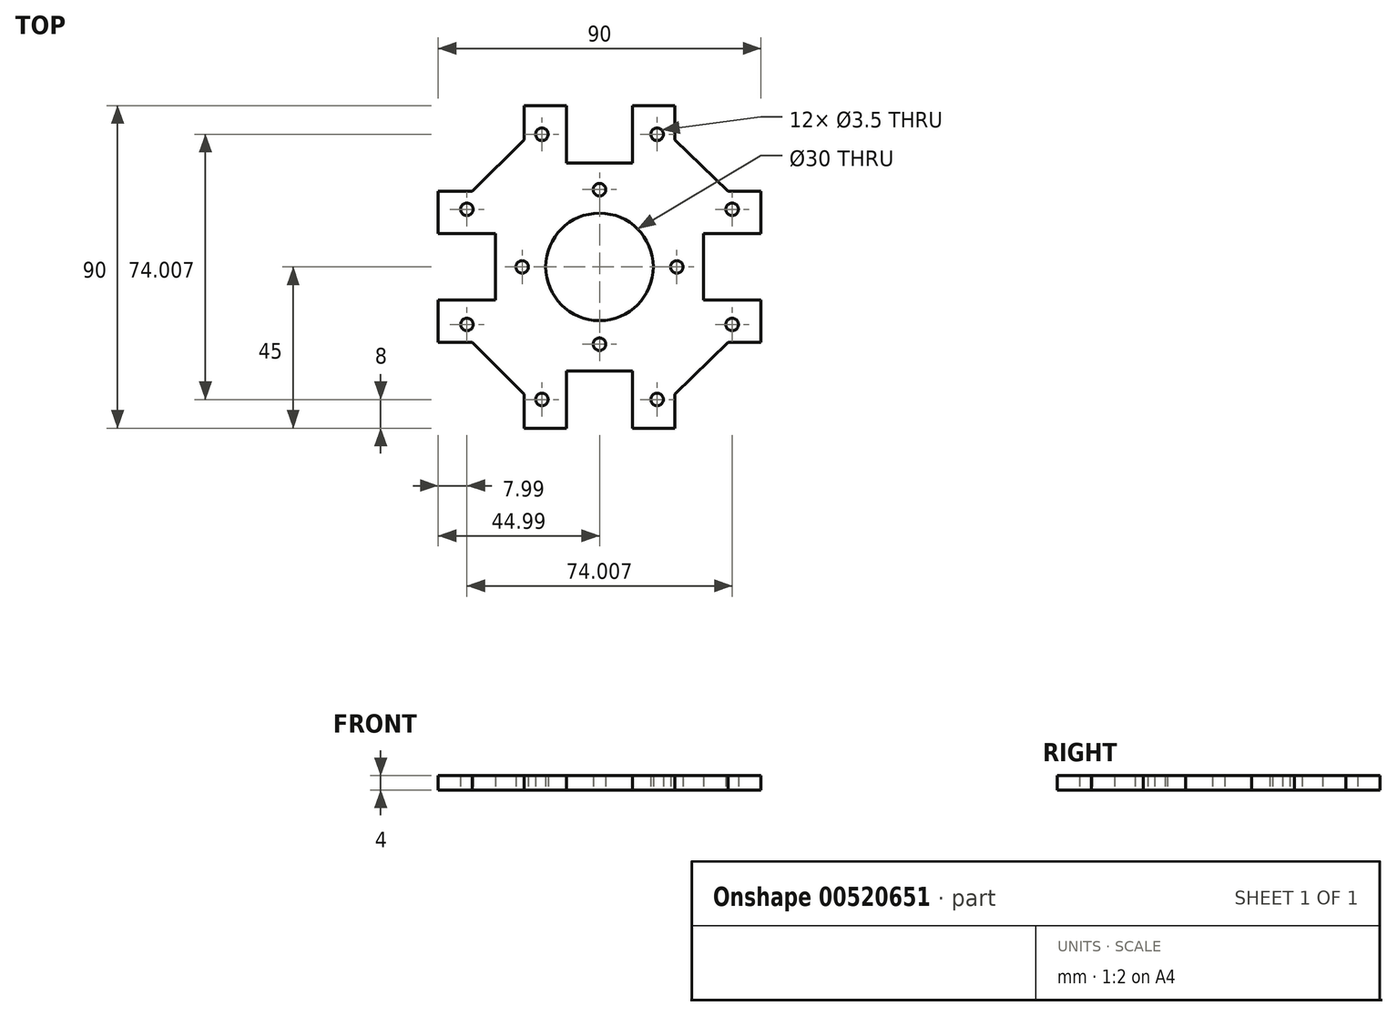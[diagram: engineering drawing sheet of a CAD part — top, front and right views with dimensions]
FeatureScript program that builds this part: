
annotation { "Feature Type Name" : "Feature", "Feature Type Description" : "" }
export const myFeature = defineFeature(function(context is Context, id is Id, definition is map)
    precondition{}
    {
        {
            var Q0;
            Q0=qCreatedBy(makeId("Top.planeOp"),FACE);
            var sketch = newSketch(context, id + "F0", { "sketchPlane" : qUnion([Q0])});
            skLineSegment(sketch, "E0.bottom", {"start": v(23.93, 0) * mm, "end": v(35.75, 0) * mm});
            skLineSegment(sketch, "E0.top", {"start": v(23.93, 90) * mm, "end": v(35.75, 90) * mm});
            skLineSegment(sketch, "E0.left", {"start": v(0, 23.93) * mm, "end": v(0, 35.75) * mm});
            skLineSegment(sketch, "E0.right", {"start": v(90, 23.93) * mm, "end": v(90, 35.75) * mm});
            skLineSegment(sketch, "E1.right", {"start": v(66.07, 80.5) * mm, "end": v(80.9, 66.07) * mm});
            skLineSegment(sketch, "E2", {"start": v(9.5, 66.07) * mm, "end": v(0, 66.07) * mm});
            skLineSegment(sketch, "E3", {"start": v(9.5, 23.93) * mm, "end": v(0, 23.93) * mm});
            skLineSegment(sketch, "E4", {"start": v(23.93, 9.5) * mm, "end": v(23.93, 0) * mm});
            skLineSegment(sketch, "E5", {"start": v(66.07, 9.5) * mm, "end": v(66.07, 0) * mm});
            skLineSegment(sketch, "E6", {"start": v(80.9, 23.93) * mm, "end": v(90, 23.93) * mm});
            skLineSegment(sketch, "E7", {"start": v(80.9, 66.07) * mm, "end": v(90, 66.07) * mm});
            skLineSegment(sketch, "E8", {"start": v(23.93, 80.5) * mm, "end": v(23.93, 90) * mm});
            skLineSegment(sketch, "E9", {"start": v(66.07, 80.5) * mm, "end": v(66.07, 90) * mm});
            skPoint(sketch, "E10.orphan", {"position": v(33.94, 90) * mm});
            skLineSegment(sketch, "E11.trimOffspring", {"start": v(66.07, 9.5) * mm, "end": v(80.9, 23.93) * mm});
            skLineSegment(sketch, "E12.trimOffspring", {"start": v(9.5, 23.93) * mm, "end": v(23.93, 9.5) * mm});
            skLineSegment(sketch, "E13.trimOffspring", {"start": v(9.5, 66.07) * mm, "end": v(23.93, 80.5) * mm});
            skCircle(sketch, "E14", {"center": v(28.93, 82) * mm, "radius": 1.75 * mm});
            skCircle(sketch, "E15", {"center": v(61.07, 82) * mm, "radius": 1.75 * mm});
            skCircle(sketch, "E16", {"center": v(8, 61.07) * mm, "radius": 1.75 * mm});
            skCircle(sketch, "E17", {"center": v(8, 28.93) * mm, "radius": 1.75 * mm});
            skCircle(sketch, "E18", {"center": v(82, 28.93) * mm, "radius": 1.75 * mm});
            skCircle(sketch, "E19", {"center": v(28.93, 8) * mm, "radius": 1.75 * mm});
            skCircle(sketch, "E20", {"center": v(61.07, 8) * mm, "radius": 1.75 * mm});
            skCircle(sketch, "E21", {"center": v(82, 61.07) * mm, "radius": 1.75 * mm});
            skPoint(sketch, "E22", {"position": v(45, 45) * mm});
            skCircle(sketch, "E23", {"center": v(45, 45) * mm, "radius": 15 * mm});
            skCircle(sketch, "E24", {"center": v(23.43, 45) * mm, "radius": 1.75 * mm});
            skCircle(sketch, "E25", {"center": v(45, 66.57) * mm, "radius": 1.75 * mm});
            skCircle(sketch, "E26", {"center": v(66.57, 45) * mm, "radius": 1.75 * mm});
            skCircle(sketch, "E27", {"center": v(45, 23.43) * mm, "radius": 1.75 * mm});
            skPoint(sketch, "E28", {"position": v(45, 16) * mm});
            skLineSegment(sketch, "E29.top", {"start": v(35.75, 16) * mm, "end": v(54.25, 16) * mm});
            skLineSegment(sketch, "E29.left", {"start": v(35.75, 0) * mm, "end": v(35.75, 16) * mm});
            skLineSegment(sketch, "E29.right", {"start": v(54.25, 0) * mm, "end": v(54.25, 16) * mm});
            skLineSegment(sketch, "E30.bottom", {"start": v(90, 54.25) * mm, "end": v(74, 54.25) * mm});
            skLineSegment(sketch, "E30.top", {"start": v(90, 35.75) * mm, "end": v(74, 35.75) * mm});
            skLineSegment(sketch, "E30.right", {"start": v(74, 54.25) * mm, "end": v(74, 35.75) * mm});
            skLineSegment(sketch, "E31.top", {"start": v(35.75, 74) * mm, "end": v(54.25, 74) * mm});
            skLineSegment(sketch, "E31.left", {"start": v(35.75, 90) * mm, "end": v(35.75, 74) * mm});
            skLineSegment(sketch, "E31.right", {"start": v(54.25, 90) * mm, "end": v(54.25, 74) * mm});
            skLineSegment(sketch, "E32.bottom", {"start": v(0, 54.25) * mm, "end": v(16, 54.25) * mm});
            skLineSegment(sketch, "E32.top", {"start": v(0, 35.75) * mm, "end": v(16, 35.75) * mm});
            skLineSegment(sketch, "E32.right", {"start": v(16, 54.25) * mm, "end": v(16, 35.75) * mm});
            skLineSegment(sketch, "E33.trimOffspring", {"start": v(54.25, 90) * mm, "end": v(66.07, 90) * mm});
            skLineSegment(sketch, "E34.trimOffspring", {"start": v(90, 54.25) * mm, "end": v(90, 66.07) * mm});
            skLineSegment(sketch, "E35.trimOffspring", {"start": v(54.25, 0) * mm, "end": v(66.07, 0) * mm});
            skPoint(sketch, "E36.center.orphan", {"position": v(45, 14) * mm});
            skLineSegment(sketch, "E37.trimOffspring", {"start": v(0, 54.25) * mm, "end": v(0, 66.07) * mm});
            skSolve(sketch);
        }
        {
            var Q0;
            Q0=makeQuery(id+"F0.imprint","IMPRINT",FACE,{"disambiguationData":[TD([[makeQuery(id+"F0.imprint","IMPRINT",EDGE,{"derivedFrom":sQuery(id+"F0.wireOp",EDGE,"E0.bottom")}),1.0]])]});
            extrude(context, id + "F1", {"entities" : qUnion([Q0]), "depth" : 4 * mm, "offsetDistance" : 25 * mm});
        }
    });
